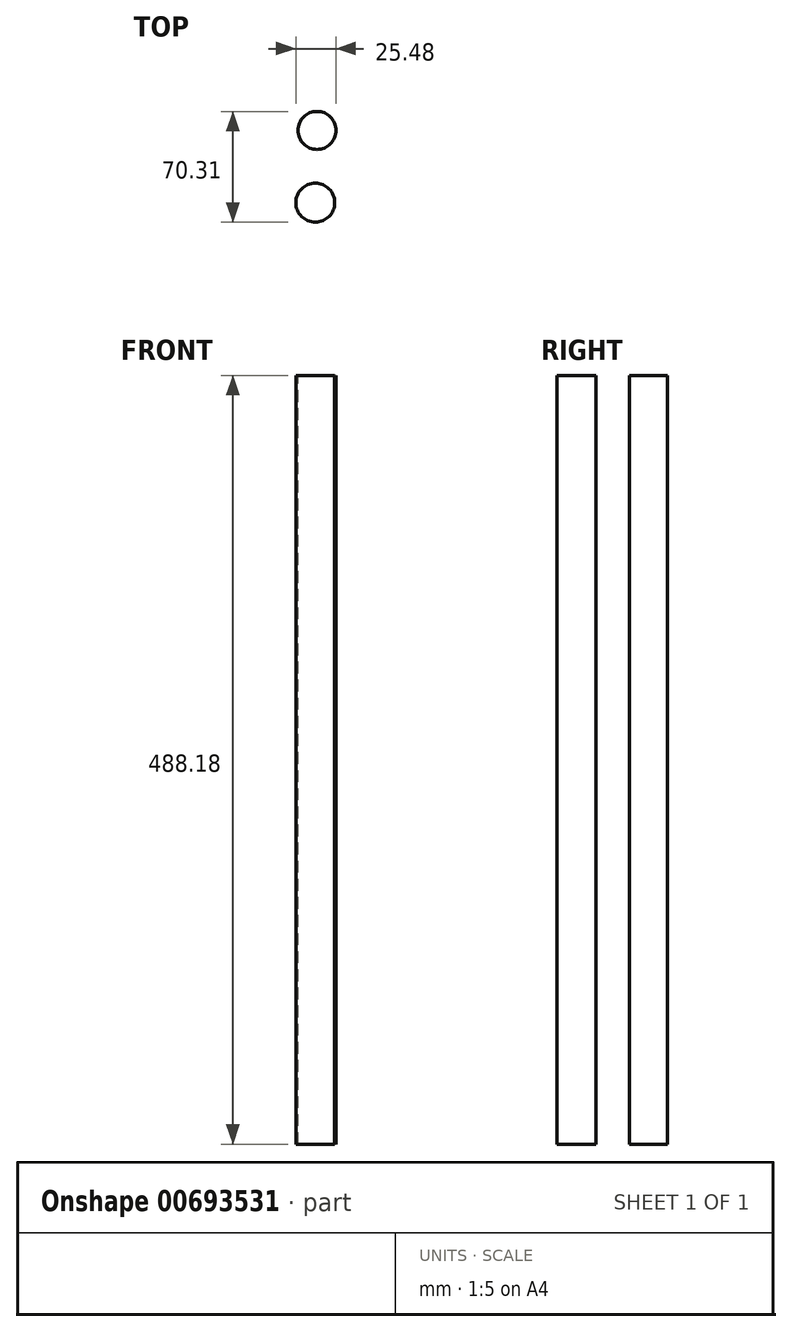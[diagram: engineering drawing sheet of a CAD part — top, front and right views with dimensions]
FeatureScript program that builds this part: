
annotation { "Feature Type Name" : "Feature", "Feature Type Description" : "" }
export const myFeature = defineFeature(function(context is Context, id is Id, definition is map)
    precondition{}
    {
        {
            var Q0;
            Q0=qCreatedBy(makeId("Top.planeOp"),FACE);
            var sketch = newSketch(context, id + "F0", { "sketchPlane" : qUnion([Q0])});
            skCircle(sketch, "E0", {"center": v(35.58, -22.8) * mm, "radius": 12.34 * mm});
            skCircle(sketch, "E1", {"center": v(36.66, 23.12) * mm, "radius": 12.06 * mm});
            skSolve(sketch);
        }
        {
            var Q0;
            Q0=sQuery(id+"F0.wireOp",EDGE,"E0");
            var Q1;
            Q1=sQuery(id+"F0.wireOp",EDGE,"E1");
            extrude(context, id + "F1", {"bodyType" : ToolBodyType.SURFACE, "surfaceEntities" : qUnion([Q0, Q1]), "depth" : 488.18 * mm, "offsetDistance" : 25.4 * mm});
        }
    });
